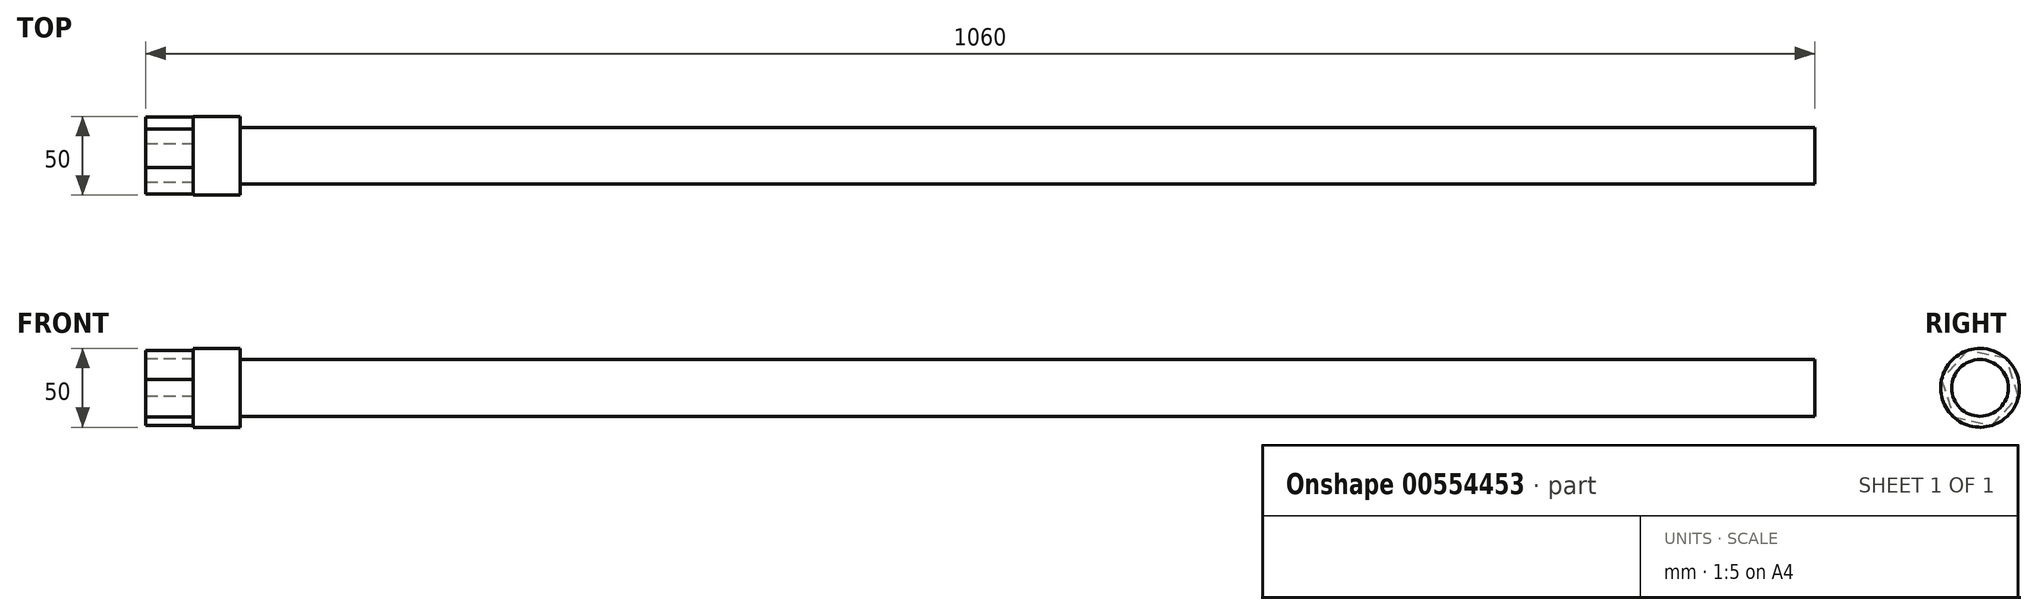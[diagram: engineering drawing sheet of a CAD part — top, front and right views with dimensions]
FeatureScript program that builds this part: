
annotation { "Feature Type Name" : "Feature", "Feature Type Description" : "" }
export const myFeature = defineFeature(function(context is Context, id is Id, definition is map)
    precondition{}
    {
        {
            var Q0;
            Q0=qCreatedBy(makeId("Right.planeOp"),FACE);
            var sketch = newSketch(context, id + "F0", { "sketchPlane" : qUnion([Q0])});
            skCircle(sketch, "E0", {"center": v(0, 0) * mm, "radius": 18 * mm});
            skSolve(sketch);
        }
        {
            var Q0;
            Q0=makeQuery(id+"F0.imprint","IMPRINT",FACE,{"disambiguationData":[TD([[makeQuery(id+"F0.imprint","IMPRINT",EDGE,{"derivedFrom":sQuery(id+"F0.wireOp",EDGE,"E0")}),1.0]])]});
            extrude(context, id + "F1", {"entities" : qUnion([Q0]), "endBound" : BoundingType.SYMMETRIC, "depth" : 1000 * mm, "offsetDistance" : 25 * mm});
        }
        {
            var Q0;
            Q0=makeQuery(id+"F1.opExtrude","CAP_FACE",FACE,{"disambiguationData":[OSD([sQuery(id+"F0.wireOp",EDGE,"E0")])],"isStart":true});
            var sketch = newSketch(context, id + "F2", { "sketchPlane" : qUnion([Q0])});
            skCircle(sketch, "E1", {"center": v(0, 0) * mm, "radius": 25 * mm});
            skSolve(sketch);
        }
        {
            var Q0;
            Q0 = qSketchRegion(id + "F2", true);
            extrude(context, id + "F3", {"entities" : qUnion([Q0]), "operationType" : NewBodyOperationType.ADD, "depth" : 30 * mm, "offsetDistance" : 25 * mm});
        }
        {
            var Q0;
            Q0=makeQuery(id+"F3.opExtrude","CAP_FACE",FACE,{"disambiguationData":[OSD([sQuery(id+"F2.wireOp",EDGE,"E1")])],"isStart":false});
            var sketch = newSketch(context, id + "F4", { "sketchPlane" : qUnion([Q0])});
            skCircle(sketch, "E2.cCircle", {"center": v(0, 0) * mm, "radius": 25 * mm, "construction": true});
            skLineSegment(sketch, "E2.0", {"start": v(16.75, -18.56) * mm, "end": v(-7.7, -23.79) * mm});
            skLineSegment(sketch, "E2.1", {"start": v(-7.7, -23.79) * mm, "end": v(-24.45, -5.23) * mm});
            skLineSegment(sketch, "E2.2", {"start": v(-24.45, -5.23) * mm, "end": v(-16.75, 18.56) * mm});
            skLineSegment(sketch, "E2.3", {"start": v(-16.75, 18.56) * mm, "end": v(7.7, 23.79) * mm});
            skLineSegment(sketch, "E2.4", {"start": v(7.7, 23.79) * mm, "end": v(24.45, 5.23) * mm});
            skLineSegment(sketch, "E2.5", {"start": v(24.45, 5.23) * mm, "end": v(16.75, -18.56) * mm});
            skSolve(sketch);
        }
        {
            var Q0;
            Q0 = qSketchRegion(id + "F4", true);
            extrude(context, id + "F5", {"entities" : qUnion([Q0]), "operationType" : NewBodyOperationType.ADD, "depth" : 30 * mm, "offsetDistance" : 25 * mm});
        }
    });
